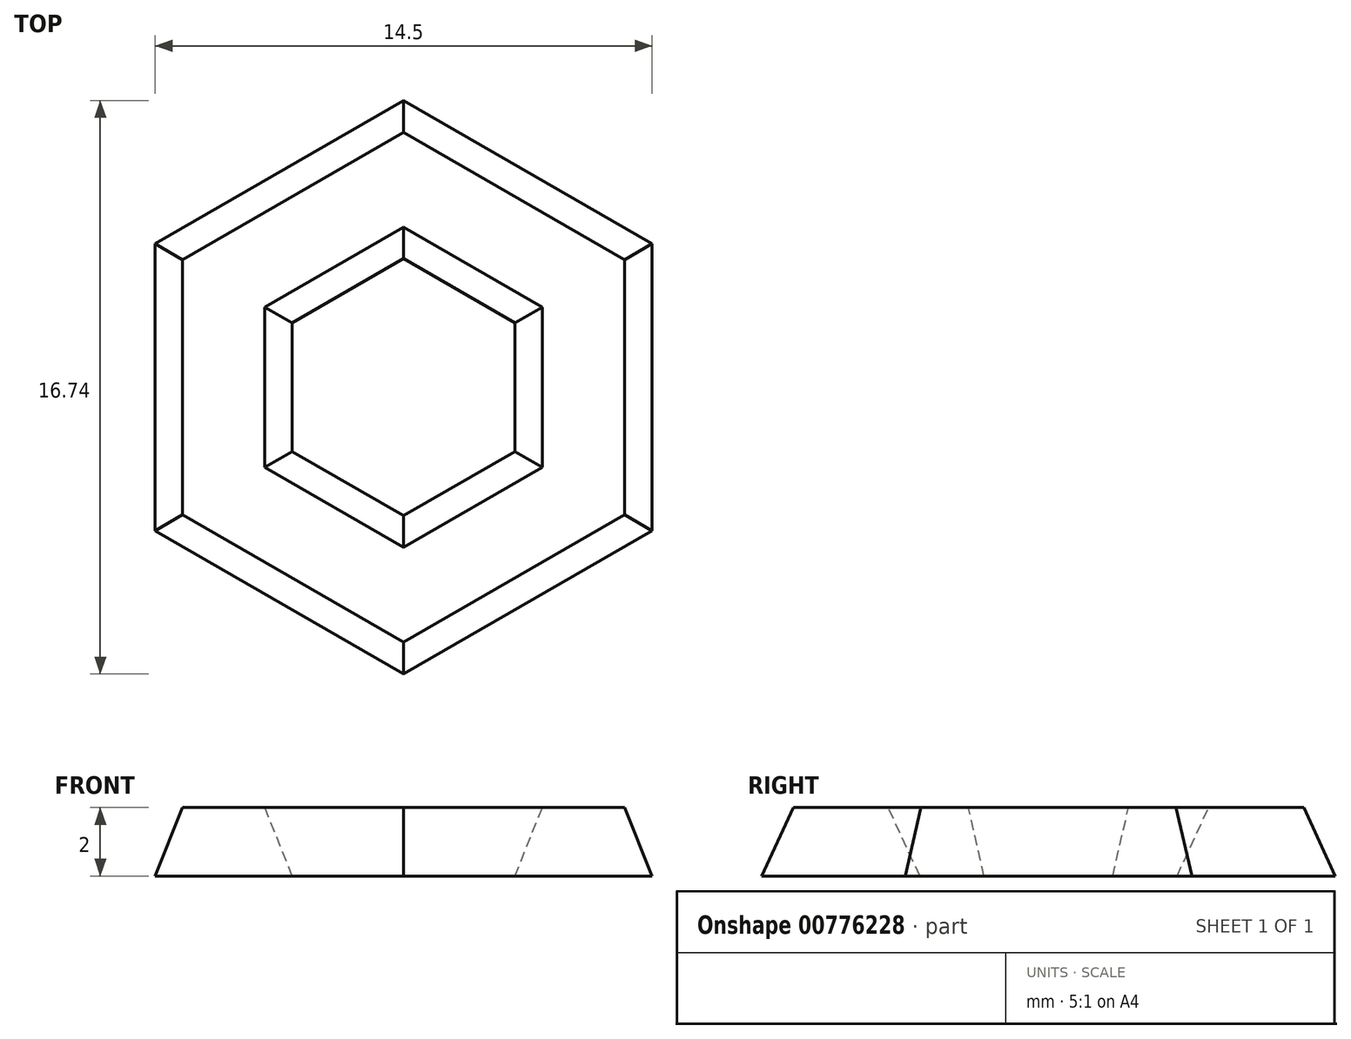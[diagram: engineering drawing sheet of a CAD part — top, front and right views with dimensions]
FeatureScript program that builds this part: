
annotation { "Feature Type Name" : "Feature", "Feature Type Description" : "" }
export const myFeature = defineFeature(function(context is Context, id is Id, definition is map)
    precondition{}
    {
        {
            var Q0;
            Q0=qCreatedBy(makeId("Top.planeOp"),FACE);
            var sketch = newSketch(context, id + "F0", { "sketchPlane" : qUnion([Q0])});
            skCircle(sketch, "E0", {"center": v(0, 0) * mm, "radius": 3.25 * mm, "construction": true});
            skLineSegment(sketch, "E1.0", {"start": v(3.25, 1.88) * mm, "end": v(3.25, -1.88) * mm});
            skLineSegment(sketch, "E1.1", {"start": v(3.25, -1.88) * mm, "end": v(0, -3.75) * mm});
            skLineSegment(sketch, "E1.2", {"start": v(0, -3.75) * mm, "end": v(-3.25, -1.88) * mm});
            skLineSegment(sketch, "E1.3", {"start": v(-3.25, -1.88) * mm, "end": v(-3.25, 1.88) * mm});
            skLineSegment(sketch, "E1.4", {"start": v(-3.25, 1.88) * mm, "end": v(0, 3.75) * mm});
            skLineSegment(sketch, "E1.5", {"start": v(0, 3.75) * mm, "end": v(3.25, 1.88) * mm});
            skPoint(sketch, "E1.0.midPoint", {"position": v(3.25, 0) * mm});
            skLineSegment(sketch, "E2.0", {"start": v(-7.25, -4.19) * mm, "end": v(-7.25, 4.19) * mm});
            skLineSegment(sketch, "E2.1", {"start": v(0, 8.37) * mm, "end": v(7.25, 4.19) * mm});
            skLineSegment(sketch, "E2.2", {"start": v(7.25, 4.19) * mm, "end": v(7.25, -4.19) * mm});
            skLineSegment(sketch, "E2.3", {"start": v(-7.25, 4.19) * mm, "end": v(0, 8.37) * mm});
            skLineSegment(sketch, "E2.4", {"start": v(7.25, -4.19) * mm, "end": v(0, -8.37) * mm});
            skLineSegment(sketch, "E2.5", {"start": v(0, -8.37) * mm, "end": v(-7.25, -4.19) * mm});
            skSolve(sketch);
        }
        {
            var Q0;
            Q0=makeQuery(id+"F0.imprint","IMPRINT",FACE,{"disambiguationData":[TD([[makeQuery(id+"F0.imprint","IMPRINT",EDGE,{"derivedFrom":sQuery(id+"F0.wireOp",EDGE,"E1.0")}),1.0]])]});
            extrude(context, id + "F1", {"entities" : qUnion([Q0]), "depth" : 2 * mm, "offsetDistance" : 25 * mm});
        }
        {
            var Q0;
            Q0=makeQuery(id+"F1.opExtrude","CAP_EDGE",EDGE,{"disambiguationData":[OSD([sQuery(id+"F0.wireOp",EDGE,"E2.0")])],"isStart":false});
            var Q1;
            Q1=makeQuery(id+"F1.opExtrude","CAP_EDGE",EDGE,{"disambiguationData":[OSD([sQuery(id+"F0.wireOp",EDGE,"E2.5")])],"isStart":false});
            var Q2;
            Q2=makeQuery(id+"F1.opExtrude","CAP_EDGE",EDGE,{"disambiguationData":[OSD([sQuery(id+"F0.wireOp",EDGE,"E2.4")])],"isStart":false});
            var Q3;
            Q3=makeQuery(id+"F1.opExtrude","CAP_EDGE",EDGE,{"disambiguationData":[OSD([sQuery(id+"F0.wireOp",EDGE,"E2.2")])],"isStart":false});
            var Q4;
            Q4=makeQuery(id+"F1.opExtrude","CAP_EDGE",EDGE,{"disambiguationData":[OSD([sQuery(id+"F0.wireOp",EDGE,"E2.1")])],"isStart":false});
            var Q5;
            Q5=makeQuery(id+"F1.opExtrude","CAP_EDGE",EDGE,{"disambiguationData":[OSD([sQuery(id+"F0.wireOp",EDGE,"E2.3")])],"isStart":false});
            var Q6;
            Q6=makeQuery(id+"F1.opExtrude","CAP_EDGE",EDGE,{"disambiguationData":[OSD([sQuery(id+"F0.wireOp",EDGE,"E1.3")])],"isStart":false});
            var Q7;
            Q7=makeQuery(id+"F1.opExtrude","CAP_EDGE",EDGE,{"disambiguationData":[OSD([sQuery(id+"F0.wireOp",EDGE,"E1.4")])],"isStart":false});
            var Q8;
            Q8=makeQuery(id+"F1.opExtrude","CAP_EDGE",EDGE,{"disambiguationData":[OSD([sQuery(id+"F0.wireOp",EDGE,"E1.5")])],"isStart":false});
            var Q9;
            Q9=makeQuery(id+"F1.opExtrude","CAP_EDGE",EDGE,{"disambiguationData":[OSD([sQuery(id+"F0.wireOp",EDGE,"E1.0")])],"isStart":false});
            var Q10;
            Q10=makeQuery(id+"F1.opExtrude","CAP_EDGE",EDGE,{"disambiguationData":[OSD([sQuery(id+"F0.wireOp",EDGE,"E1.1")])],"isStart":false});
            var Q11;
            Q11=makeQuery(id+"F1.opExtrude","CAP_EDGE",EDGE,{"disambiguationData":[OSD([sQuery(id+"F0.wireOp",EDGE,"E1.2")])],"isStart":false});
            chamfer(context, id + "F2", {"entities" : qUnion([Q0, Q1, Q2, Q3, Q4, Q5, Q6, Q7, Q8, Q9, Q10, Q11]), "chamferType" : ChamferType.TWO_OFFSETS, "width1" : 2 * mm, "oppositeDirection" : false, "width2" : (0.4 * 2) * mm, "tangentPropagation" : true});
        }
    });
